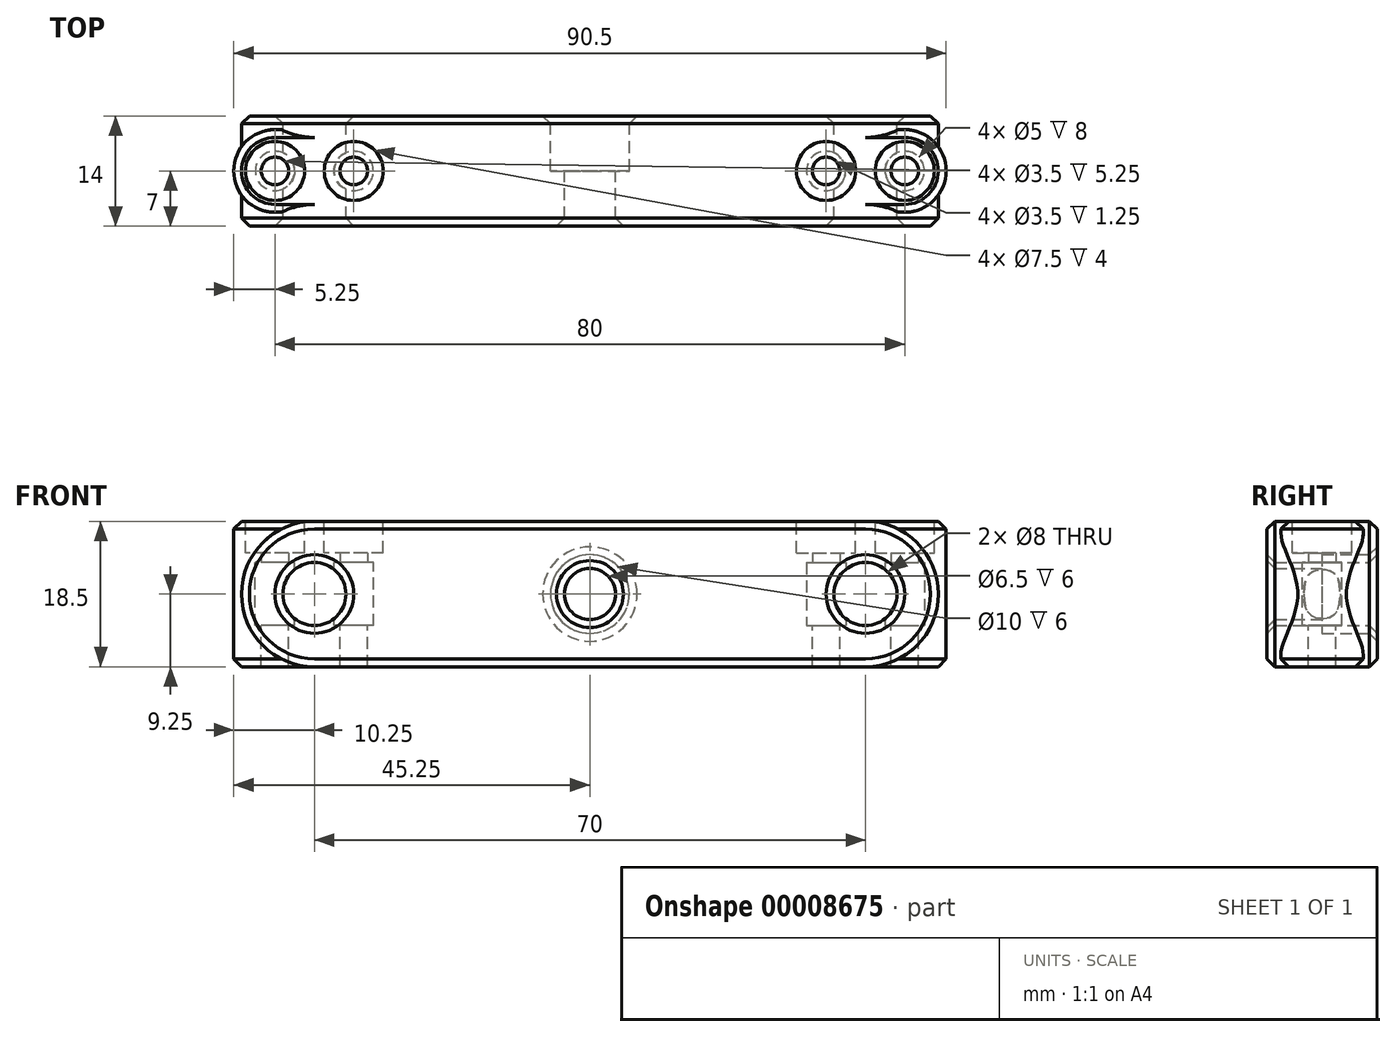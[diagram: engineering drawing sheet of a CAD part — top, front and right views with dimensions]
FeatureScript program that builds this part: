
annotation { "Feature Type Name" : "Feature", "Feature Type Description" : "" }
export const myFeature = defineFeature(function(context is Context, id is Id, definition is map)
    precondition{}
    {
        {
            var Q0;
            Q0=qCreatedBy(makeId("Front.planeOp"),FACE);
            var sketch = newSketch(context, id + "F0", { "sketchPlane" : qUnion([Q0])});
            skCircle(sketch, "E0", {"center": v(-35, 0) * mm, "radius": 4 * mm});
            skCircle(sketch, "E1", {"center": v(-35, 0) * mm, "radius": 9.25 * mm});
            skLineSegment(sketch, "E2", {"start": v(-44.25, 0) * mm, "end": v(0, 0) * mm});
            skLineSegment(sketch, "E3", {"start": v(-35, 9.25) * mm, "end": v(0, 9.25) * mm});
            skLineSegment(sketch, "E4", {"start": v(0, 0) * mm, "end": v(0, 9.25) * mm});
            skPoint(sketch, "E5", {"position": v(-35, -9.25) * mm});
            skSolve(sketch);
        }
        {
            var Q0;
            {var subQ0=sQuery(id+"F0.wireOp",EDGE,"E2");var subQ1=sQuery(id+"F0.wireOp",EDGE,"E0");var subQ2=makeQuery(id+"F0.imprint","INTERSECT",VERTEX,{"disambiguationData":[OD(0.0)],"derivedFrom":[subQ1,subQ0]});Q0=makeQuery(id+"F0.imprint","IMPRINT",FACE,{"disambiguationData":[TD([[makeQuery(id+"F0.imprint","IMPRINT",EDGE,{"disambiguationData":[TD([[subQ2,1.0]])],"derivedFrom":subQ1}),-1.0]])]});}
            var Q1;
            {var subQ1=sQuery(id+"F0.wireOp",EDGE,"E3");Q1=makeQuery(id+"F0.imprint","IMPRINT",FACE,{"disambiguationData":[TD([[makeQuery(id+"F0.imprint","IMPRINT",EDGE,{"derivedFrom":subQ1}),-1.0]])]});}
            var Q2;
            {var subQ0=sQuery(id+"F0.wireOp",EDGE,"E2");var subQ1=sQuery(id+"F0.wireOp",EDGE,"E0");var subQ3=makeQuery(id+"F0.imprint","INTERSECT",VERTEX,{"disambiguationData":[OD(0.0)],"derivedFrom":[subQ1,subQ0]});Q2=makeQuery(id+"F0.imprint","IMPRINT",FACE,{"disambiguationData":[TD([[makeQuery(id+"F0.imprint","IMPRINT",EDGE,{"disambiguationData":[TD([[subQ3,1.0]])],"derivedFrom":subQ1}),1.0]])]});}
            var Q3;
            {var subQ0=sQuery(id+"F0.wireOp",EDGE,"4a1d1f9b-7086-409e-91a0-7c4572efc49e");var subQ1=sQuery(id+"F0.wireOp",EDGE,"E2");var subQ3=makeQuery(id+"F0.imprint","INTERSECT",VERTEX,{"disambiguationData":[OD(0.0)],"derivedFrom":[subQ1,subQ0]});Q3=makeQuery(id+"F0.imprint","IMPRINT",FACE,{"disambiguationData":[TD([[makeQuery(id+"F0.imprint","IMPRINT",EDGE,{"disambiguationData":[TD([[subQ3,-1.0]])],"derivedFrom":subQ1}),1.0]])]});}
            extrude(context, id + "F1", {"entities" : qUnion([Q0, Q1, Q2, Q3]), "depth" : 14 * mm, "symmetric" : true});
        }
        {
            var Q0;
            Q0=qCreatedBy(makeId("Top.planeOp"),FACE);
            var sketch = newSketch(context, id + "F2", { "sketchPlane" : qUnion([Q0])});
            skLineSegment(sketch, "E6.0", {"start": v(-31, 0) * mm, "end": v(-39, 0) * mm, "construction": true});
            skLineSegment(sketch, "E7.0", {"start": v(-35, 7) * mm, "end": v(-44.25, 7) * mm, "construction": true});
            skLineSegment(sketch, "E8.0", {"start": v(-35, -7) * mm, "end": v(-44.25, -7) * mm, "construction": true});
            skLineSegment(sketch, "E9.0", {"start": v(-35, -7) * mm, "end": v(0, -7) * mm, "construction": true});
            skLineSegment(sketch, "E10.0", {"start": v(-35, 7) * mm, "end": v(0, 7) * mm, "construction": true});
            skLineSegment(sketch, "E11", {"start": v(-39, 7) * mm, "end": v(-39, -7) * mm, "construction": true});
            skLineSegment(sketch, "E12", {"start": v(-31, 7) * mm, "end": v(-31, -7) * mm, "construction": true});
            skLineSegment(sketch, "E13", {"start": v(-35, 7) * mm, "end": v(-35, -7) * mm, "construction": true});
            skCircle(sketch, "E14", {"center": v(-40, 0) * mm, "radius": 1.75 * mm});
            skCircle(sketch, "E15", {"center": v(-30, 0) * mm, "radius": 1.75 * mm});
            skCircle(sketch, "E16", {"center": v(-30, 0) * mm, "radius": 2.5 * mm});
            skCircle(sketch, "E17", {"center": v(-40, 0) * mm, "radius": 2.5 * mm});
            skPoint(sketch, "E18", {"position": v(-38.25, 0) * mm});
            skCircle(sketch, "E19", {"center": v(-40, 0) * mm, "radius": 5.25 * mm});
            skCircle(sketch, "E20", {"center": v(-30, 0) * mm, "radius": 5.25 * mm});
            skCircle(sketch, "E21", {"center": v(-40, 0) * mm, "radius": 3.75 * mm});
            skCircle(sketch, "E22", {"center": v(-30, 0) * mm, "radius": 3.75 * mm});
            skLineSegment(sketch, "E23", {"start": v(-40, -5.25) * mm, "end": v(-35, -5.25) * mm});
            skLineSegment(sketch, "E24", {"start": v(-40, 5.25) * mm, "end": v(-35, 5.25) * mm});
            skLineSegment(sketch, "E25", {"start": v(-35, 5.25) * mm, "end": v(-35, -5.25) * mm});
            skSolve(sketch);
        }
        {
            var Q0;
            Q0=makeQuery(id+"F2.imprint","IMPRINT",FACE,{"disambiguationData":[TD([[makeQuery(id+"F2.imprint","IMPRINT",EDGE,{"derivedFrom":sQuery(id+"F2.wireOp",EDGE,"E19")}),1.0]])]});
            var Q1;
            Q1=makeQuery(id+"F2.imprint","IMPRINT",FACE,{"disambiguationData":[TD([[makeQuery(id+"F2.imprint","IMPRINT",EDGE,{"derivedFrom":sQuery(id+"F2.wireOp",EDGE,"E20")}),1.0]])]});
            var Q2;
            Q2=makeQuery(id+"F2.imprint","IMPRINT",FACE,{"disambiguationData":[TD([[makeQuery(id+"F2.imprint","IMPRINT",EDGE,{"derivedFrom":sQuery(id+"F2.wireOp",EDGE,"E17")}),-1.0]])]});
            var Q3;
            Q3=makeQuery(id+"F2.imprint","IMPRINT",FACE,{"disambiguationData":[TD([[makeQuery(id+"F2.imprint","IMPRINT",EDGE,{"derivedFrom":sQuery(id+"F2.wireOp",EDGE,"E14")}),-1.0]])]});
            var Q4;
            Q4=makeQuery(id+"F2.imprint","IMPRINT",FACE,{"disambiguationData":[TD([[makeQuery(id+"F2.imprint","IMPRINT",EDGE,{"derivedFrom":sQuery(id+"F2.wireOp",EDGE,"E14")}),1.0]])]});
            var Q5;
            Q5=makeQuery(id+"F2.imprint","IMPRINT",FACE,{"disambiguationData":[TD([[makeQuery(id+"F2.imprint","IMPRINT",EDGE,{"derivedFrom":sQuery(id+"F2.wireOp",EDGE,"E15")}),1.0]])]});
            var Q6;
            Q6=makeQuery(id+"F2.imprint","IMPRINT",FACE,{"disambiguationData":[TD([[makeQuery(id+"F2.imprint","IMPRINT",EDGE,{"derivedFrom":sQuery(id+"F2.wireOp",EDGE,"E15")}),-1.0]])]});
            var Q7;
            Q7=makeQuery(id+"F2.imprint","IMPRINT",FACE,{"disambiguationData":[TD([[makeQuery(id+"F2.imprint","IMPRINT",EDGE,{"derivedFrom":sQuery(id+"F2.wireOp",EDGE,"E16")}),-1.0]])]});
            var Q8;
            {var subQ3=sQuery(id+"F2.wireOp",EDGE,"E23");Q8=makeQuery(id+"F2.imprint","IMPRINT",FACE,{"disambiguationData":[TD([[makeQuery(id+"F2.imprint","IMPRINT",EDGE,{"derivedFrom":subQ3}),1.0]])]});}
            var Q9;
            {var subQ3=sQuery(id+"F2.wireOp",EDGE,"E24");Q9=makeQuery(id+"F2.imprint","IMPRINT",FACE,{"disambiguationData":[TD([[makeQuery(id+"F2.imprint","IMPRINT",EDGE,{"derivedFrom":subQ3}),-1.0]])]});}
            var Q10;
            Q10=makeQuery(id+"F1.opExtrude","SWEPT_FACE",FACE,{"disambiguationData":[OSD([sQuery(id+"F0.wireOp",EDGE,"E3")])]});
            extrude(context, id + "F3", {"entities" : qUnion([Q0, Q1, Q2, Q3, Q4, Q5, Q6, Q7, Q8, Q9]), "operationType" : NewBodyOperationType.ADD, "endBound" : BoundingType.UP_TO_SURFACE, "endBoundEntityFace" : qUnion([Q10]), "depth" : 8.5 * mm});
        }
        {
            var Q0;
            Q0=makeQuery(id+"F2.imprint","IMPRINT",FACE,{"disambiguationData":[TD([[makeQuery(id+"F2.imprint","IMPRINT",EDGE,{"derivedFrom":sQuery(id+"F2.wireOp",EDGE,"E14")}),1.0]])]});
            var Q1;
            Q1=makeQuery(id+"F2.imprint","IMPRINT",FACE,{"disambiguationData":[TD([[makeQuery(id+"F2.imprint","IMPRINT",EDGE,{"derivedFrom":sQuery(id+"F2.wireOp",EDGE,"E15")}),1.0]])]});
            extrude(context, id + "F4", {"entities" : qUnion([Q0, Q1]), "operationType" : NewBodyOperationType.REMOVE, "depth" : 25 * mm});
        }
        {
            var Q0;
            Q0=makeQuery(id+"F2.imprint","IMPRINT",FACE,{"disambiguationData":[TD([[makeQuery(id+"F2.imprint","IMPRINT",EDGE,{"derivedFrom":sQuery(id+"F2.wireOp",EDGE,"E14")}),-1.0]])]});
            var Q1;
            Q1=makeQuery(id+"F2.imprint","IMPRINT",FACE,{"disambiguationData":[TD([[makeQuery(id+"F2.imprint","IMPRINT",EDGE,{"derivedFrom":sQuery(id+"F2.wireOp",EDGE,"E14")}),1.0]])]});
            var Q2;
            Q2=makeQuery(id+"F2.imprint","IMPRINT",FACE,{"disambiguationData":[TD([[makeQuery(id+"F2.imprint","IMPRINT",EDGE,{"derivedFrom":sQuery(id+"F2.wireOp",EDGE,"E15")}),1.0]])]});
            var Q3;
            Q3=makeQuery(id+"F2.imprint","IMPRINT",FACE,{"disambiguationData":[TD([[makeQuery(id+"F2.imprint","IMPRINT",EDGE,{"derivedFrom":sQuery(id+"F2.wireOp",EDGE,"E15")}),-1.0]])]});
            extrude(context, id + "F5", {"entities" : qUnion([Q0, Q1, Q2, Q3]), "operationType" : NewBodyOperationType.REMOVE, "depth" : 4 * mm});
        }
        {
            var Q0;
            {var subQ0=sQuery(id+"F0.wireOp",EDGE,"E2");var subQ1=sQuery(id+"F0.wireOp",EDGE,"E0");var subQ3=makeQuery(id+"F0.imprint","INTERSECT",VERTEX,{"disambiguationData":[OD(0.0)],"derivedFrom":[subQ1,subQ0]});Q0=makeQuery(id+"F0.imprint","IMPRINT",FACE,{"disambiguationData":[TD([[makeQuery(id+"F0.imprint","IMPRINT",EDGE,{"disambiguationData":[TD([[subQ3,1.0]])],"derivedFrom":subQ1}),1.0]])]});}
            extrude(context, id + "F6", {"entities" : qUnion([Q0]), "operationType" : NewBodyOperationType.REMOVE, "depth" : 25 * mm, "symmetric" : true});
        }
        {
            var Q0;
            Q0=makeQuery(id+"F1.opExtrude","SWEPT_BODY",BODY,{"disambiguationData":[OSD([sQuery(id+"F0.wireOp",EDGE,"E1"),sQuery(id+"F0.wireOp",EDGE,"E2"),sQuery(id+"F0.wireOp",EDGE,"E3"),sQuery(id+"F0.wireOp",EDGE,"E4")])]});
            var Q1;
            Q1=qCreatedBy(makeId("Top.planeOp"),FACE);
            mirror(context, id + "F7", {"entities" : qUnion([Q0]), "mirrorPlane" : qUnion([Q1])});
        }
        {
            var Q0;
            Q0=makeQuery(id+"F1.opExtrude","SWEPT_FACE",FACE,{"disambiguationData":[OSD([sQuery(id+"F0.wireOp",EDGE,"E3")])]});
            var sketch = newSketch(context, id + "F8", { "sketchPlane" : qUnion([Q0])});
            skCircle(sketch, "E26.0.0", {"center": v(-40, 0) * mm, "radius": 5.25 * mm});
            skCircle(sketch, "E27.0", {"center": v(-30, 0) * mm, "radius": 1.75 * mm});
            skCircle(sketch, "E28", {"center": v(-30, 0) * mm, "radius": 3.75 * mm});
            skCircle(sketch, "E29", {"center": v(-40, 0) * mm, "radius": 3.75 * mm});
            skSolve(sketch);
        }
        {
            var Q0;
            Q0=makeQuery(id+"F8.imprint","IMPRINT",FACE,{"disambiguationData":[TD([[makeQuery(id+"F8.imprint","IMPRINT",EDGE,{"derivedFrom":sQuery(id+"F8.wireOp",EDGE,"E29")}),1.0]])]});
            var Q1;
            Q1=makeQuery(id+"F8.imprint","IMPRINT",FACE,{"disambiguationData":[TD([[makeQuery(id+"F8.imprint","IMPRINT",EDGE,{"derivedFrom":sQuery(id+"F8.wireOp",EDGE,"E27.0")}),1.0]])]});
            extrude(context, id + "F9", {"entities" : qUnion([Q0, Q1]), "operationType" : NewBodyOperationType.REMOVE, "oppositeDirection" : true, "depth" : 4 * mm});
        }
        {
            var Q0;
            Q0=makeQuery(id+"F1.opExtrude","SWEPT_BODY",BODY,{"disambiguationData":[OSD([sQuery(id+"F0.wireOp",EDGE,"E1"),sQuery(id+"F0.wireOp",EDGE,"E2"),sQuery(id+"F0.wireOp",EDGE,"E3"),sQuery(id+"F0.wireOp",EDGE,"E4")])]});
            var Q1;
            Q1=makeQuery(id+"F7.opPattern","COPY",BODY,{"derivedFrom":makeQuery(id+"F1.opExtrude","SWEPT_BODY",BODY,{"disambiguationData":[OSD([sQuery(id+"F0.wireOp",EDGE,"E1"),sQuery(id+"F0.wireOp",EDGE,"E2"),sQuery(id+"F0.wireOp",EDGE,"E3"),sQuery(id+"F0.wireOp",EDGE,"E4")])]}),"instanceName":"1"});
            var Q2;
            Q2=qCreatedBy(makeId("Right.planeOp"),FACE);
            mirror(context, id + "F10", {"entities" : qUnion([Q0, Q1]), "mirrorPlane" : qUnion([Q2])});
        }
        {
            var Q0;
            Q0=makeQuery(id+"F7.opPattern","COPY",BODY,{"derivedFrom":makeQuery(id+"F1.opExtrude","SWEPT_BODY",BODY,{"disambiguationData":[OSD([sQuery(id+"F0.wireOp",EDGE,"E1"),sQuery(id+"F0.wireOp",EDGE,"E2"),sQuery(id+"F0.wireOp",EDGE,"E3"),sQuery(id+"F0.wireOp",EDGE,"E4")])]}),"instanceName":"1"});
            var Q1;
            Q1=makeQuery(id+"F10.opPattern","COPY",BODY,{"derivedFrom":makeQuery(id+"F1.opExtrude","SWEPT_BODY",BODY,{"disambiguationData":[OSD([sQuery(id+"F0.wireOp",EDGE,"E1"),sQuery(id+"F0.wireOp",EDGE,"E2"),sQuery(id+"F0.wireOp",EDGE,"E3"),sQuery(id+"F0.wireOp",EDGE,"E4")])]}),"instanceName":"1"});
            var Q2;
            Q2=makeQuery(id+"F1.opExtrude","SWEPT_BODY",BODY,{"disambiguationData":[OSD([sQuery(id+"F0.wireOp",EDGE,"E1"),sQuery(id+"F0.wireOp",EDGE,"E2"),sQuery(id+"F0.wireOp",EDGE,"E3"),sQuery(id+"F0.wireOp",EDGE,"E4")])]});
            var Q3;
            Q3=makeQuery(id+"F10.opPattern","COPY",BODY,{"derivedFrom":makeQuery(id+"F7.opPattern","COPY",BODY,{"derivedFrom":makeQuery(id+"F1.opExtrude","SWEPT_BODY",BODY,{"disambiguationData":[OSD([sQuery(id+"F0.wireOp",EDGE,"E1"),sQuery(id+"F0.wireOp",EDGE,"E2"),sQuery(id+"F0.wireOp",EDGE,"E3"),sQuery(id+"F0.wireOp",EDGE,"E4")])]}),"instanceName":"1"}),"instanceName":"1"});
            booleanBodies(context, id + "F11", {"operationType" : BooleanOperationType.UNION, "tools" : qUnion([Q0, Q1, Q2, Q3])});
        }
        {
            var Q0;
            {var subQ0=makeQuery(id+"F1.opExtrude","CAP_FACE",FACE,{"disambiguationData":[OSD([sQuery(id+"F0.wireOp",EDGE,"E1"),sQuery(id+"F0.wireOp",EDGE,"E2"),sQuery(id+"F0.wireOp",EDGE,"E3"),sQuery(id+"F0.wireOp",EDGE,"E4")])],"isStart":true});var subQ1=makeQuery(id+"F7.opPattern","COPY",FACE,{"derivedFrom":subQ0,"instanceName":"1"});Q0=makeQuery(id+"F11.opBoolean","MERGE",FACE,{"derivedFrom":[subQ0,subQ1,makeQuery(id+"F10.opPattern","COPY",FACE,{"derivedFrom":subQ0,"instanceName":"1"}),makeQuery(id+"F10.opPattern","COPY",FACE,{"derivedFrom":subQ1,"instanceName":"1"})]});}
            var sketch = newSketch(context, id + "F12", { "sketchPlane" : qUnion([Q0])});
            skCircle(sketch, "E30", {"center": v(0, 0) * mm, "radius": 5 * mm});
            skCircle(sketch, "E31", {"center": v(0, 0) * mm, "radius": 3.25 * mm});
            skSolve(sketch);
        }
        {
            var Q0;
            Q0=makeQuery(id+"F12.imprint","IMPRINT",FACE,{"disambiguationData":[TD([[makeQuery(id+"F12.imprint","IMPRINT",EDGE,{"derivedFrom":sQuery(id+"F12.wireOp",EDGE,"E31")}),1.0]])]});
            extrude(context, id + "F13", {"entities" : qUnion([Q0]), "operationType" : NewBodyOperationType.REMOVE, "endBound" : BoundingType.THROUGH_ALL, "oppositeDirection" : true, "depth" : 25 * mm});
        }
        {
            var Q0;
            Q0=makeQuery(id+"F12.imprint","IMPRINT",FACE,{"disambiguationData":[TD([[makeQuery(id+"F12.imprint","IMPRINT",EDGE,{"derivedFrom":sQuery(id+"F12.wireOp",EDGE,"E30")}),1.0]])]});
            extrude(context, id + "F14", {"entities" : qUnion([Q0]), "operationType" : NewBodyOperationType.REMOVE, "oppositeDirection" : true, "depth" : 7 * mm});
        }
        {
            var Q0;
            {var subQ0=makeQuery(id+"F1.opExtrude","CAP_FACE",FACE,{"disambiguationData":[OSD([sQuery(id+"F0.wireOp",EDGE,"E1"),sQuery(id+"F0.wireOp",EDGE,"E2"),sQuery(id+"F0.wireOp",EDGE,"E3"),sQuery(id+"F0.wireOp",EDGE,"E4")])],"isStart":false});var subQ1=makeQuery(id+"F7.opPattern","COPY",FACE,{"derivedFrom":subQ0,"instanceName":"1"});Q0=makeQuery(id+"F11.opBoolean","MERGE",FACE,{"derivedFrom":[subQ0,subQ1,makeQuery(id+"F10.opPattern","COPY",FACE,{"derivedFrom":subQ0,"instanceName":"1"}),makeQuery(id+"F10.opPattern","COPY",FACE,{"derivedFrom":subQ1,"instanceName":"1"})]});}
            var Q1;
            {var subQ0=makeQuery(id+"F1.opExtrude","CAP_FACE",FACE,{"disambiguationData":[OSD([sQuery(id+"F0.wireOp",EDGE,"E1"),sQuery(id+"F0.wireOp",EDGE,"E2"),sQuery(id+"F0.wireOp",EDGE,"E3"),sQuery(id+"F0.wireOp",EDGE,"E4")])],"isStart":true});var subQ1=makeQuery(id+"F7.opPattern","COPY",FACE,{"derivedFrom":subQ0,"instanceName":"1"});Q1=makeQuery(id+"F11.opBoolean","MERGE",FACE,{"derivedFrom":[subQ0,subQ1,makeQuery(id+"F10.opPattern","COPY",FACE,{"derivedFrom":subQ0,"instanceName":"1"}),makeQuery(id+"F10.opPattern","COPY",FACE,{"derivedFrom":subQ1,"instanceName":"1"})]});}
            var Q2;
            Q2=makeQuery(id+"F3.opExtrude","CAP_EDGE",EDGE,{"disambiguationData":[OSD([sQuery(id+"F2.wireOp",EDGE,"E23")])],"isStart":false});
            var Q3;
            Q3=makeQuery(id+"F10.opPattern","COPY",EDGE,{"derivedFrom":makeQuery(id+"F3.opExtrude","CAP_EDGE",EDGE,{"disambiguationData":[OSD([sQuery(id+"F2.wireOp",EDGE,"E19")])],"isStart":false}),"instanceName":"1"});
            var Q4;
            Q4=makeQuery(id+"F7.opPattern","COPY",EDGE,{"derivedFrom":makeQuery(id+"F3.opExtrude","CAP_EDGE",EDGE,{"disambiguationData":[OSD([sQuery(id+"F2.wireOp",EDGE,"E19")])],"isStart":false}),"instanceName":"1"});
            var Q5;
            Q5=makeQuery(id+"F10.opPattern","COPY",EDGE,{"derivedFrom":makeQuery(id+"F7.opPattern","COPY",EDGE,{"derivedFrom":makeQuery(id+"F3.opExtrude","CAP_EDGE",EDGE,{"disambiguationData":[OSD([sQuery(id+"F2.wireOp",EDGE,"E19")])],"isStart":false}),"instanceName":"1"}),"instanceName":"1"});
            chamfer(context, id + "F15", {"entities" : qUnion([Q0, Q1, Q2, Q3, Q4, Q5]), "width" : 1 * mm, "tangentPropagation" : true});
        }
    });
